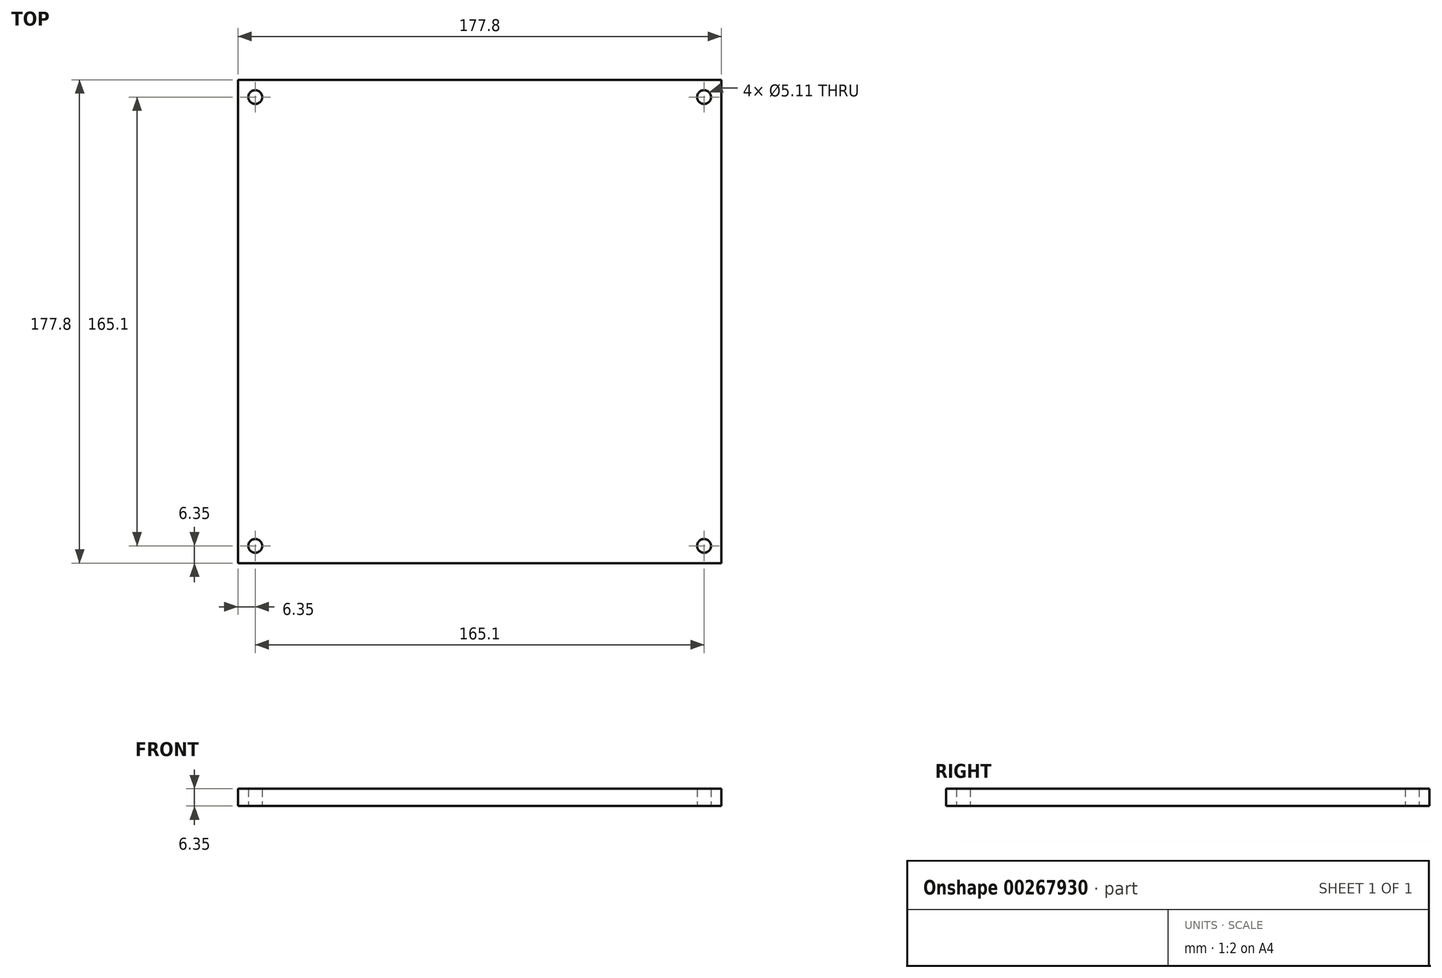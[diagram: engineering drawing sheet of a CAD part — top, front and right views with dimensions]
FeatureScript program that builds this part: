
annotation { "Feature Type Name" : "Feature", "Feature Type Description" : "" }
export const myFeature = defineFeature(function(context is Context, id is Id, definition is map)
    precondition{}
    {
        {
            var Q0;
            Q0=qCreatedBy(makeId("Top.planeOp"),FACE);
            var sketch = newSketch(context, id + "F0", { "sketchPlane" : qUnion([Q0])});
            skLineSegment(sketch, "E0.bottom", {"start": v(-76.2, 76.2) * mm, "end": v(76.2, 76.2) * mm});
            skLineSegment(sketch, "E0.top", {"start": v(-76.2, -76.2) * mm, "end": v(76.2, -76.2) * mm});
            skLineSegment(sketch, "E0.left", {"start": v(-76.2, 76.2) * mm, "end": v(-76.2, -76.2) * mm});
            skLineSegment(sketch, "E0.right", {"start": v(76.2, 76.2) * mm, "end": v(76.2, -76.2) * mm});
            skPoint(sketch, "E0.middle", {"position": v(0, 0) * mm});
            skLineSegment(sketch, "E1.bottom", {"start": v(-88.9, 88.9) * mm, "end": v(88.9, 88.9) * mm});
            skLineSegment(sketch, "E1.top", {"start": v(-88.9, -88.9) * mm, "end": v(88.9, -88.9) * mm});
            skLineSegment(sketch, "E1.left", {"start": v(-88.9, 88.9) * mm, "end": v(-88.9, -88.9) * mm});
            skLineSegment(sketch, "E1.right", {"start": v(88.9, 88.9) * mm, "end": v(88.9, -88.9) * mm});
            skLineSegment(sketch, "E2.bottom", {"start": v(-82.55, 82.55) * mm, "end": v(82.55, 82.55) * mm, "construction": true});
            skLineSegment(sketch, "E2.top", {"start": v(-82.55, -82.55) * mm, "end": v(82.55, -82.55) * mm, "construction": true});
            skLineSegment(sketch, "E2.left", {"start": v(-82.55, 82.55) * mm, "end": v(-82.55, -82.55) * mm, "construction": true});
            skLineSegment(sketch, "E2.right", {"start": v(82.55, 82.55) * mm, "end": v(82.55, -82.55) * mm, "construction": true});
            skCircle(sketch, "E3", {"center": v(-82.55, 82.55) * mm, "radius": 2.55 * mm});
            skCircle(sketch, "E4", {"center": v(82.55, 82.55) * mm, "radius": 2.55 * mm});
            skCircle(sketch, "E5", {"center": v(-82.55, -82.55) * mm, "radius": 2.55 * mm});
            skCircle(sketch, "E6", {"center": v(82.55, -82.55) * mm, "radius": 2.55 * mm});
            skSolve(sketch);
        }
        {
            var Q0;
            Q0=makeQuery(id+"F0.imprint","IMPRINT",FACE,{"disambiguationData":[TD([[makeQuery(id+"F0.imprint","IMPRINT",EDGE,{"derivedFrom":sQuery(id+"F0.wireOp",EDGE,"E0.bottom")}),-1.0]])]});
            var Q1;
            Q1=makeQuery(id+"F0.imprint","IMPRINT",FACE,{"disambiguationData":[TD([[makeQuery(id+"F0.imprint","IMPRINT",EDGE,{"derivedFrom":sQuery(id+"F0.wireOp",EDGE,"E0.bottom")}),1.0]])]});
            extrude(context, id + "F1", {"entities" : qUnion([Q0, Q1]), "depth" : 6.35 * mm, "offsetDistance" : 25.4 * mm});
        }
    });
